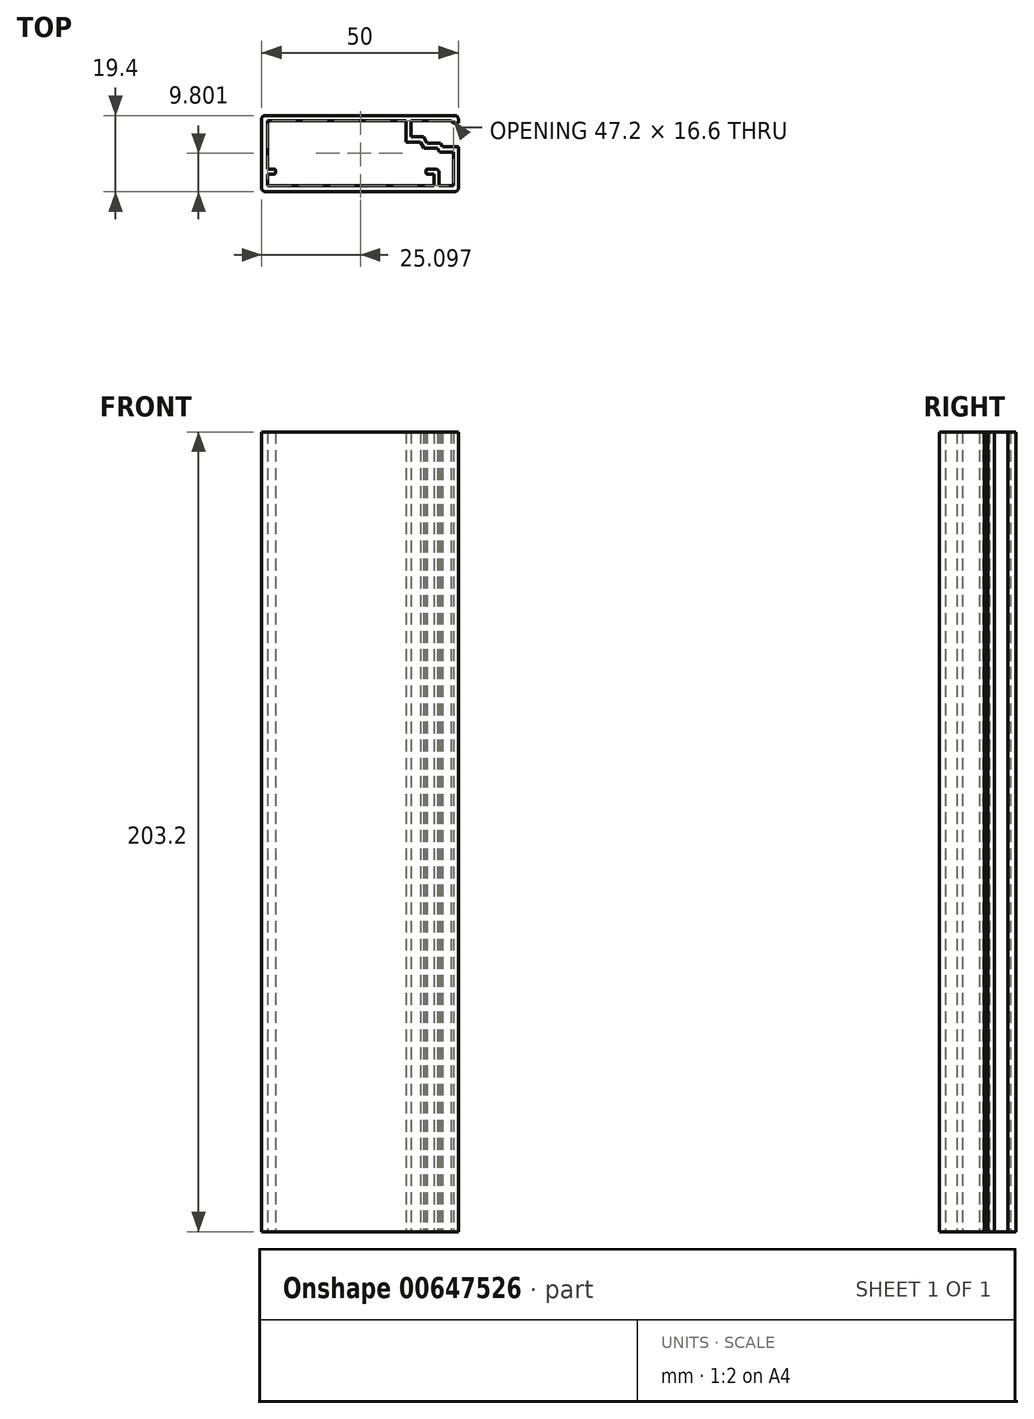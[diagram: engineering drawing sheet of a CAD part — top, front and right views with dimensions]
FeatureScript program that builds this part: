
annotation { "Feature Type Name" : "Feature", "Feature Type Description" : "" }
export const myFeature = defineFeature(function(context is Context, id is Id, definition is map)
    precondition{}
    {
        {
            var Q0;
            Q0=qCreatedBy(makeId("Top.planeOp"),FACE);
            var sketch = newSketch(context, id + "F0", { "sketchPlane" : qUnion([Q0])});
            skLineSegment(sketch, "E0.0.1", {"start": v(9.29, 59.67) * mm, "end": v(9.29, 63.8) * mm});
            skLineSegment(sketch, "E0.0.2", {"start": v(20.09, 63.1) * mm, "end": v(21.29, 63.1) * mm});
            skLineSegment(sketch, "E0.0.3", {"start": v(21.29, 63.1) * mm, "end": v(21.29, 64.1) * mm});
            skArc(sketch, "E0.0.4", {"start": v(21.29, 64.1) * mm, "mid": v(21, 64.8) * mm, "end": v(20.29, 65.1) * mm});
            skLineSegment(sketch, "E0.0.5", {"start": v(20.29, 65.1) * mm, "end": v(-27.71, 65.1) * mm});
            skArc(sketch, "E0.0.6", {"start": v(-27.71, 65.1) * mm, "mid": v(-28.42, 64.8) * mm, "end": v(-28.71, 64.1) * mm});
            skLineSegment(sketch, "E0.0.7", {"start": v(-28.71, 64.1) * mm, "end": v(-28.71, 46.7) * mm});
            skArc(sketch, "E0.0.8", {"start": v(-28.71, 46.7) * mm, "mid": v(-28.42, 46) * mm, "end": v(-27.71, 45.7) * mm});
            skLineSegment(sketch, "E0.0.9", {"start": v(-27.71, 45.7) * mm, "end": v(20.29, 45.7) * mm});
            skArc(sketch, "E0.0.10", {"start": v(20.29, 45.7) * mm, "mid": v(21, 46) * mm, "end": v(21.29, 46.7) * mm});
            skLineSegment(sketch, "E0.0.11", {"start": v(21.29, 46.7) * mm, "end": v(21.29, 57.13) * mm});
            skLineSegment(sketch, "E1.0", {"start": v(-27.21, 63.8) * mm, "end": v(7.99, 63.8) * mm});
            skLineSegment(sketch, "E2.0", {"start": v(7.99, 63.8) * mm, "end": v(7.99, 58.37) * mm});
            skLineSegment(sketch, "E3.0", {"start": v(19.99, 55.83) * mm, "end": v(19.99, 47.2) * mm});
            skLineSegment(sketch, "E4.0", {"start": v(19.99, 47.2) * mm, "end": v(16.39, 47.2) * mm});
            skLineSegment(sketch, "E5.0", {"start": v(16.39, 47.2) * mm, "end": v(16.39, 50.5) * mm});
            skArc(sketch, "E6.0", {"start": v(16.39, 50.5) * mm, "mid": v(16.1, 51.2) * mm, "end": v(15.39, 51.5) * mm});
            skLineSegment(sketch, "E7.0", {"start": v(15.39, 51.5) * mm, "end": v(13.39, 51.5) * mm});
            skArc(sketch, "E8.0", {"start": v(13.39, 51.5) * mm, "mid": v(13.17, 51.41) * mm, "end": v(13.09, 51.2) * mm});
            skLineSegment(sketch, "E9.0", {"start": v(13.09, 51.2) * mm, "end": v(13.09, 50.5) * mm});
            skArc(sketch, "E10.0", {"start": v(13.09, 50.5) * mm, "mid": v(13.17, 50.29) * mm, "end": v(13.39, 50.2) * mm});
            skLineSegment(sketch, "E11.0", {"start": v(13.39, 50.2) * mm, "end": v(15.09, 50.2) * mm});
            skLineSegment(sketch, "E12.0", {"start": v(15.09, 50.2) * mm, "end": v(15.09, 47.2) * mm});
            skLineSegment(sketch, "E13.0", {"start": v(15.09, 47.2) * mm, "end": v(-27.21, 47.2) * mm});
            skLineSegment(sketch, "E14.0", {"start": v(-27.21, 47.2) * mm, "end": v(-27.21, 50.2) * mm});
            skLineSegment(sketch, "E15.0", {"start": v(-27.21, 50.2) * mm, "end": v(-25.51, 50.2) * mm});
            skArc(sketch, "E16.0", {"start": v(-25.51, 50.2) * mm, "mid": v(-25.3, 50.29) * mm, "end": v(-25.21, 50.5) * mm});
            skLineSegment(sketch, "E17.0", {"start": v(-25.21, 50.5) * mm, "end": v(-25.21, 51.2) * mm});
            skArc(sketch, "E18.0", {"start": v(-25.21, 51.2) * mm, "mid": v(-25.3, 51.41) * mm, "end": v(-25.51, 51.5) * mm});
            skLineSegment(sketch, "E19.0", {"start": v(-25.51, 51.5) * mm, "end": v(-27.21, 51.5) * mm});
            skLineSegment(sketch, "E20.0", {"start": v(-27.21, 51.5) * mm, "end": v(-27.21, 63.8) * mm});
            skLineSegment(sketch, "E21", {"start": v(9.29, 59.67) * mm, "end": v(12.37, 59.67) * mm});
            skLineSegment(sketch, "E22", {"start": v(12.37, 59.67) * mm, "end": v(13.29, 58.08) * mm});
            skLineSegment(sketch, "E23", {"start": v(13.29, 58.08) * mm, "end": v(16.74, 58.08) * mm});
            skLineSegment(sketch, "E24", {"start": v(16.74, 58.08) * mm, "end": v(17.29, 57.13) * mm});
            skLineSegment(sketch, "E25", {"start": v(17.29, 57.13) * mm, "end": v(21.29, 57.13) * mm});
            skLineSegment(sketch, "E26", {"start": v(7.99, 58.37) * mm, "end": v(11.62, 58.37) * mm});
            skLineSegment(sketch, "E27", {"start": v(11.62, 58.37) * mm, "end": v(12.54, 56.78) * mm});
            skLineSegment(sketch, "E28", {"start": v(12.54, 56.78) * mm, "end": v(15.99, 56.78) * mm});
            skLineSegment(sketch, "E29", {"start": v(15.99, 56.78) * mm, "end": v(16.54, 55.83) * mm});
            skLineSegment(sketch, "E30", {"start": v(16.54, 55.83) * mm, "end": v(19.99, 55.83) * mm});
            skLineSegment(sketch, "E31", {"start": v(20.09, 63.1) * mm, "end": v(19.39, 63.8) * mm});
            skLineSegment(sketch, "E32", {"start": v(19.39, 63.8) * mm, "end": v(9.29, 63.8) * mm});
            skSolve(sketch);
        }
        {
            var Q0;
            Q0=makeQuery(id+"F0.imprint","IMPRINT",FACE,{"disambiguationData":[TD([[makeQuery(id+"F0.imprint","IMPRINT",EDGE,{"derivedFrom":sQuery(id+"F0.wireOp",EDGE,"E0.0.1")}),1.0]])]});
            extrude(context, id + "F1", {"entities" : qUnion([Q0]), "depth" : 203.2 * mm, "offsetDistance" : 25 * mm});
        }
    });
